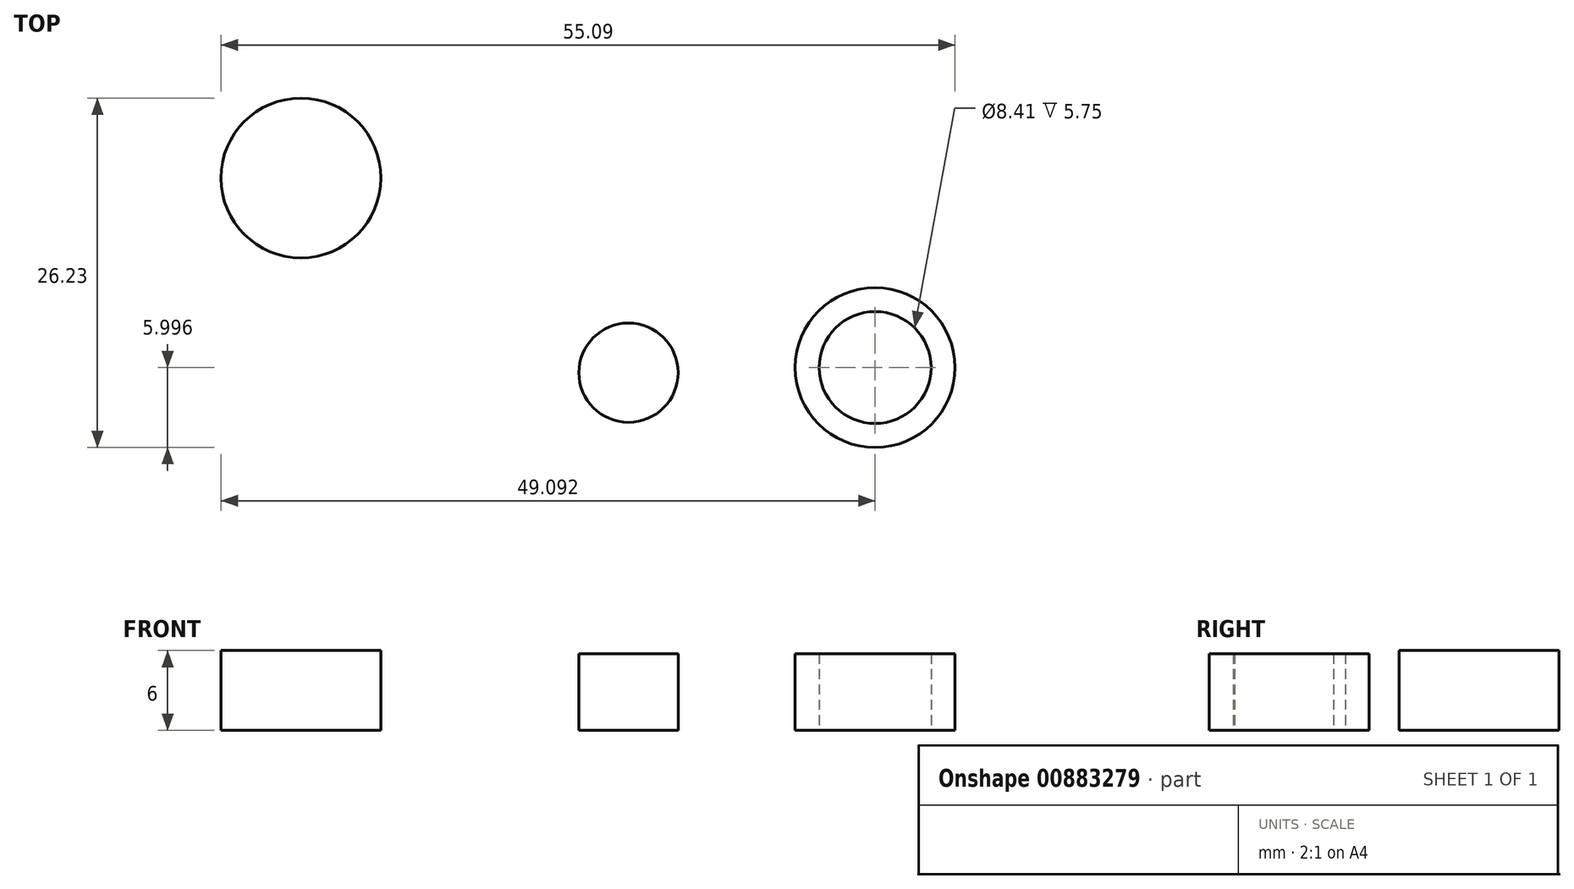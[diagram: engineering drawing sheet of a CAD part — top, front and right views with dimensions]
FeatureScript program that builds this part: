
annotation { "Feature Type Name" : "Feature", "Feature Type Description" : "" }
export const myFeature = defineFeature(function(context is Context, id is Id, definition is map)
    precondition{}
    {
        {
            var Q0;
            Q0=qCreatedBy(makeId("Top.planeOp"),FACE);
            var sketch = newSketch(context, id + "F0", { "sketchPlane" : qUnion([Q0])});
            skCircle(sketch, "E0", {"center": v(-44.73, 33.48) * mm, "radius": 6 * mm});
            skSolve(sketch);
        }
        {
            var Q0;
            Q0 = qSketchRegion(id + "F0", true);
            extrude(context, id + "F1", {"entities" : qUnion([Q0]), "depth" : 6 * mm, "offsetDistance" : 25 * mm});
        }
        {
            var Q0;
            Q0=qCreatedBy(makeId("Top.planeOp"),FACE);
            var sketch = newSketch(context, id + "F2", { "sketchPlane" : qUnion([Q0])});
            skCircle(sketch, "E1", {"center": v(-1.64, 19.25) * mm, "radius": 6 * mm});
            skCircle(sketch, "E2", {"center": v(-1.64, 19.25) * mm, "radius": 4.2 * mm});
            skCircle(sketch, "E3", {"center": v(-20.15, 18.86) * mm, "radius": 3.73 * mm});
            skSolve(sketch);
        }
        {
            var Q0;
            Q0 = qSketchRegion(id + "F2", true);
            extrude(context, id + "F3", {"entities" : qUnion([Q0]), "depth" : 5.75 * mm, "offsetDistance" : 25 * mm});
        }
    });
